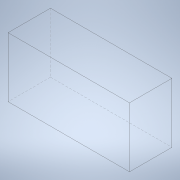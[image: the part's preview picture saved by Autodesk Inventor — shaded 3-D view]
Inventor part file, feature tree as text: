
AUTODESK INVENTOR PART (.ipt)
format: ipt  version: 2022 (Build 260153000, 153)  size: 97,792 bytes
history: native  units: in
note: dims shown in document units (in); Inventor stores cm internally (conversion verified against a paired STEP export)
features: other x1, extrude x1, sketch x1
ambient origin geometry x8: Origin, YZ Plane, XZ Plane, XY Plane, X Axis, Y Axis, Z Axis, Center Point
bodies: Body1 (feature_tree)
feature tree (3):
  other  "Water"
  extrude  "Extrusion1"  Depth=46.5in
  sketch  "Sketch1"  dims[d0=94.5in d1=46.5in d2=33.0in d3=0.0in]
